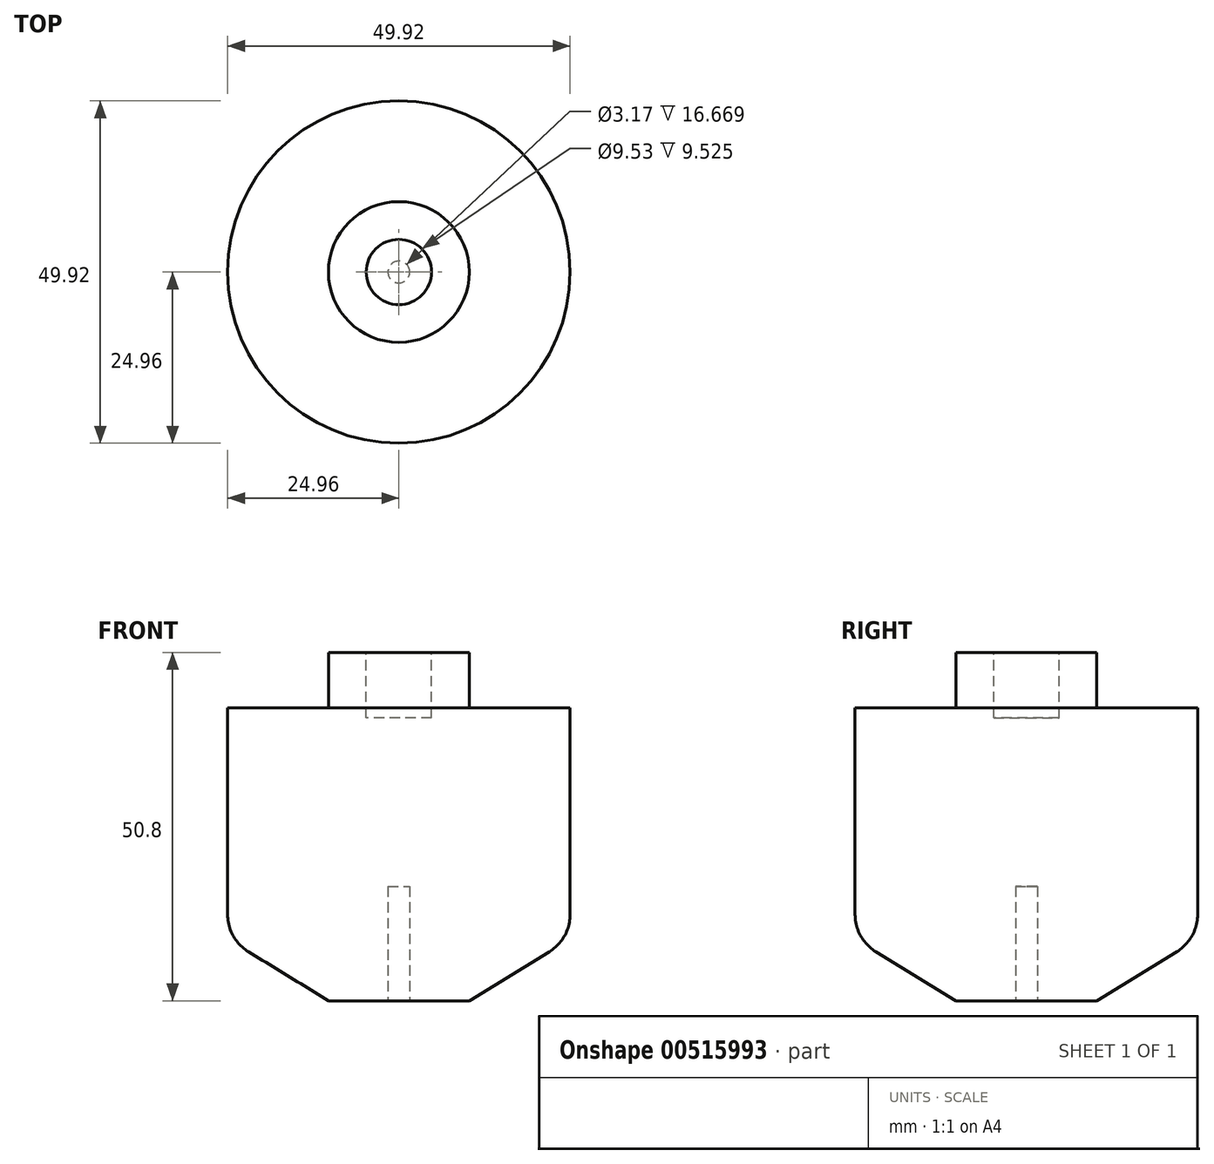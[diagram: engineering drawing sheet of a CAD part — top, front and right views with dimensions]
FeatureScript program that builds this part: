
annotation { "Feature Type Name" : "Feature", "Feature Type Description" : "" }
export const myFeature = defineFeature(function(context is Context, id is Id, definition is map)
    precondition{}
    {
        {
            var Q0;
            Q0=qCreatedBy(makeId("Front.planeOp"),FACE);
            var sketch = newSketch(context, id + "F0", { "sketchPlane" : qUnion([Q0])});
            skLineSegment(sketch, "E0", {"start": v(0, 0) * mm, "end": v(0, 50.8) * mm});
            skLineSegment(sketch, "E1", {"start": v(0, 0) * mm, "end": v(10.26, 0) * mm});
            skLineSegment(sketch, "E2", {"start": v(10.26, 0) * mm, "end": v(21.93, 7.15) * mm});
            skLineSegment(sketch, "E3", {"start": v(24.96, 12.57) * mm, "end": v(24.96, 17.33) * mm});
            skLineSegment(sketch, "E4", {"start": v(24.96, 17.33) * mm, "end": v(10.26, 17.33) * mm});
            skLineSegment(sketch, "E5", {"start": v(10.26, 17.33) * mm, "end": v(10.26, 50.8) * mm});
            skLineSegment(sketch, "E6", {"start": v(10.26, 50.8) * mm, "end": v(0, 50.8) * mm});
            skPoint(sketch, "E7.visualSharp", {"position": v(24.96, 9.01) * mm});
            skArc(sketch, "E7.filletArc", {"start": v(21.93, 7.15) * mm, "mid": v(24.15, 9.47) * mm, "end": v(24.96, 12.57) * mm});
            skSolve(sketch);
        }
        {
            var Q0;
            Q0=makeQuery(id+"F0.imprint","IMPRINT",FACE,{"disambiguationData":[TD([[makeQuery(id+"F0.imprint","IMPRINT",EDGE,{"derivedFrom":sQuery(id+"F0.wireOp",EDGE,"E0")}),-1.0]])]});
            var Q1;
            Q1=sQuery(id+"F0.wireOp",EDGE,"E0");
            revolve(context, id + "F1", {"entities" : qUnion([Q0]), "axis" : qUnion([Q1]), "revolveType" : RevolveType.FULL});
        }
        {
            var Q0;
            Q0=makeQuery(id+"F1.opRevolve","SWEPT_FACE",FACE,{"disambiguationData":[OSD([sQuery(id+"F0.wireOp",EDGE,"E6")])]});
            var sketch = newSketch(context, id + "F2", { "sketchPlane" : qUnion([Q0])});
            skCircle(sketch, "E8", {"center": v(0, 0) * mm, "radius": 4.76 * mm});
            skSolve(sketch);
        }
        {
            var Q0;
            Q0=makeQuery(id+"F2.imprint","IMPRINT",FACE,{"disambiguationData":[TD([[makeQuery(id+"F2.imprint","IMPRINT",EDGE,{"derivedFrom":sQuery(id+"F2.wireOp",EDGE,"E8")}),1.0]])]});
            extrude(context, id + "F3", {"entities" : qUnion([Q0]), "operationType" : NewBodyOperationType.REMOVE, "oppositeDirection" : true, "depth" : 9.52 * mm});
        }
        {
            var Q0;
            Q0=makeQuery(id+"F1.opRevolve","SWEPT_FACE",FACE,{"disambiguationData":[OSD([sQuery(id+"F0.wireOp",EDGE,"E1")])]});
            var sketch = newSketch(context, id + "F4", { "sketchPlane" : qUnion([Q0])});
            skCircle(sketch, "E9", {"center": v(0, 0) * mm, "radius": 1.59 * mm});
            skSolve(sketch);
        }
        {
            var Q0;
            Q0=qSketchRegion(id+"F4",true);
            extrude(context, id + "F5", {"entities" : qUnion([Q0]), "operationType" : NewBodyOperationType.REMOVE, "oppositeDirection" : true, "depth" : 16.67 * mm});
        }
        {
            var Q0;
            Q0=makeQuery(id+"F1.opRevolve","SWEPT_FACE",FACE,{"disambiguationData":[OSD([sQuery(id+"F0.wireOp",EDGE,"E4")])]});
            extrude(context, id + "F6", {"entities" : qUnion([Q0]), "operationType" : NewBodyOperationType.ADD, "depth" : 25.4 * mm});
        }
    });
